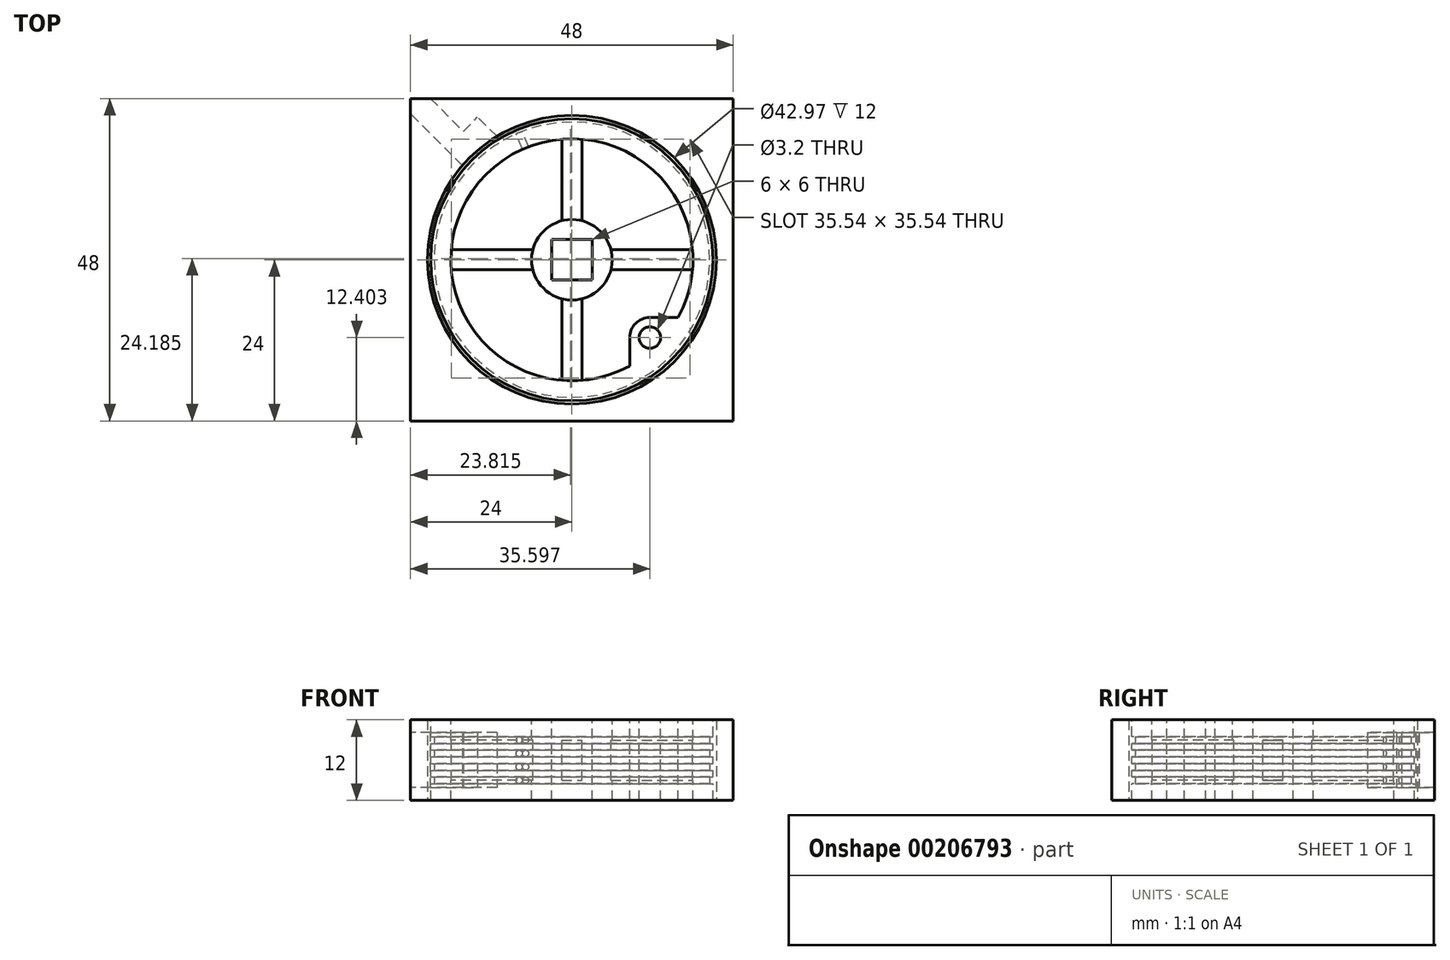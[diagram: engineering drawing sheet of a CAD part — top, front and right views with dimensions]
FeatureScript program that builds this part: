
annotation { "Feature Type Name" : "Feature", "Feature Type Description" : "" }
export const myFeature = defineFeature(function(context is Context, id is Id, definition is map)
    precondition{}
    {
        {
            var Q0;
            Q0=qCreatedBy(makeId("Front.planeOp"),FACE);
            var sketch = newSketch(context, id + "F0", { "sketchPlane" : qUnion([Q0])});
            skLineSegment(sketch, "E0", {"start": v(0, 69.7) * mm, "end": v(0, -33.75) * mm, "construction": true});
            skSolve(sketch);
        }
        {
            var Q0;
            Q0=sQuery(id+"F0.wireOp",EDGE,"E0");
            cPlane(context, id + "F1", {"entities" : qUnion([Q0]), "cplaneType" : CPlaneType.LINE_ANGLE, "offset" : 25 * mm, "angle" : 45 * degree, "width" : 150 * mm, "height" : 150 * mm});
        }
        {
            var Q0;
            Q0=qCreatedBy(makeId("Top.planeOp"),FACE);
            var sketch = newSketch(context, id + "F2", { "sketchPlane" : qUnion([Q0])});
            skCircle(sketch, "E1", {"center": v(0, 0) * mm, "radius": 21 * mm, "construction": true});
            skLineSegment(sketch, "E2.bottom", {"start": v(-24, 24) * mm, "end": v(24, 24) * mm, "construction": true});
            skLineSegment(sketch, "E2.top", {"start": v(-24, -24) * mm, "end": v(24, -24) * mm, "construction": true});
            skLineSegment(sketch, "E2.left", {"start": v(-24, 24) * mm, "end": v(-24, -24) * mm, "construction": true});
            skLineSegment(sketch, "E2.right", {"start": v(24, 24) * mm, "end": v(24, -24) * mm, "construction": true});
            skLineSegment(sketch, "E3", {"start": v(-58.08, 0) * mm, "end": v(67.15, 0) * mm, "construction": true});
            skLineSegment(sketch, "E4", {"start": v(0, 56.42) * mm, "end": v(0, -59.69) * mm, "construction": true});
            skPoint(sketch, "E5", {"position": v(21, 0) * mm});
            skSolve(sketch);
        }
        {
            var Q0;
            Q0=qCreatedBy(makeId("Top.planeOp"),FACE);
            var sketch = newSketch(context, id + "F3", { "sketchPlane" : qUnion([Q0])});
            skLineSegment(sketch, "E6.0", {"start": v(-24, 24) * mm, "end": v(24, 24) * mm});
            skLineSegment(sketch, "E6.1", {"start": v(-24, 24) * mm, "end": v(-24, -24) * mm});
            skLineSegment(sketch, "E6.2", {"start": v(-24, -24) * mm, "end": v(24, -24) * mm});
            skLineSegment(sketch, "E6.3", {"start": v(24, 24) * mm, "end": v(24, -24) * mm});
            skCircle(sketch, "E7", {"center": v(0, 0) * mm, "radius": 21.48 * mm});
            skLineSegment(sketch, "E8", {"start": v(-24, 24) * mm, "end": v(24, -24) * mm, "construction": true});
            skPoint(sketch, "E9", {"position": v(-15.2, 15.2) * mm});
            skSolve(sketch);
        }
        {
            var Q0;
            Q0=makeQuery(id+"F3.imprint","IMPRINT",FACE,{"disambiguationData":[TD([[makeQuery(id+"F3.imprint","IMPRINT",EDGE,{"derivedFrom":sQuery(id+"F3.wireOp",EDGE,"E6.0")}),-1.0]])]});
            extrude(context, id + "F4", {"entities" : qUnion([Q0]), "depth" : 12 * mm});
        }
        {
            var Q0;
            Q0=qCreatedBy(id+"F1.planeOp",FACE);
            var Q1;
            Q1=sQuery(id+"F3.wireOp",VERTEX,"E9");
            cPlane(context, id + "F5", {"entities" : qUnion([Q0, Q1]), "cplaneType" : CPlaneType.PLANE_POINT, "offset" : 25 * mm, "width" : 150 * mm, "height" : 150 * mm});
        }
        {
            var Q0;
            Q0=qCreatedBy(id+"F5.planeOp",FACE);
            cPlane(context, id + "F6", {"entities" : qUnion([Q0]), "cplaneType" : CPlaneType.OFFSET, "offset" : 3.45 * mm, "width" : 150 * mm, "height" : 150 * mm});
        }
        {
            var Q0;
            Q0=qCreatedBy(id+"F6.planeOp",FACE);
            var sketch = newSketch(context, id + "F7", { "sketchPlane" : qUnion([Q0])});
            skLineSegment(sketch, "E10.bottom", {"start": v(1.6, 10.1) * mm, "end": v(-5.1, 10.1) * mm});
            skLineSegment(sketch, "E10.top", {"start": v(1.6, 1.9) * mm, "end": v(-5.1, 1.9) * mm});
            skLineSegment(sketch, "E10.left", {"start": v(1.6, 10.1) * mm, "end": v(1.6, 1.9) * mm});
            skLineSegment(sketch, "E10.right", {"start": v(-5.1, 10.1) * mm, "end": v(-5.1, 1.9) * mm});
            skLineSegment(sketch, "E11", {"start": v(0, 12.62) * mm, "end": v(0, -16.36) * mm, "construction": true});
            skLineSegment(sketch, "E12", {"start": v(12.81, 6) * mm, "end": v(-12.63, 6) * mm, "construction": true});
            skSolve(sketch);
        }
        {
            var Q0;
            Q0 = qSketchRegion(id + "F7", true);
            var Q1;
            Q1=makeQuery(id+"F4.opExtrude","SWEPT_FACE",FACE,{"disambiguationData":[OSD([sQuery(id+"F3.wireOp",EDGE,"E7")])]});
            extrude(context, id + "F8", {"entities" : qUnion([Q0]), "operationType" : NewBodyOperationType.REMOVE, "endBound" : BoundingType.UP_TO_SURFACE, "oppositeDirection" : true, "endBoundEntityFace" : qUnion([Q1]), "depth" : 25 * mm});
        }
        {
            var Q0;
            Q0=makeQuery(id+"F8.boolean.opBoolean","COPY",FACE,{"derivedFrom":makeQuery(id+"F8.opExtrude","CAP_FACE",FACE,{"disambiguationData":[OSD([sQuery(id+"F7.wireOp",EDGE,"E10.bottom"),sQuery(id+"F7.wireOp",EDGE,"E10.top"),sQuery(id+"F7.wireOp",EDGE,"E10.left"),sQuery(id+"F7.wireOp",EDGE,"E10.right")])],"isStart":true})});
            var sketch = newSketch(context, id + "F9", { "sketchPlane" : qUnion([Q0])});
            skLineSegment(sketch, "E13.bottom", {"start": v(-1.6, 10.1) * mm, "end": v(2.1, 10.1) * mm});
            skLineSegment(sketch, "E13.top", {"start": v(-1.6, 1.9) * mm, "end": v(2.1, 1.9) * mm});
            skLineSegment(sketch, "E13.left", {"start": v(-1.6, 10.1) * mm, "end": v(-1.6, 1.9) * mm});
            skLineSegment(sketch, "E13.right", {"start": v(2.1, 10.1) * mm, "end": v(2.1, 1.9) * mm});
            skSolve(sketch);
        }
        {
            var Q0;
            Q0 = qSketchRegion(id + "F9", true);
            extrude(context, id + "F10", {"entities" : qUnion([Q0]), "operationType" : NewBodyOperationType.REMOVE, "endBound" : BoundingType.THROUGH_ALL, "oppositeDirection" : true, "depth" : 25 * mm});
        }
        {
            var Q0;
            Q0=qCreatedBy(makeId("Front.planeOp"),FACE);
            var sketch = newSketch(context, id + "F11", { "sketchPlane" : qUnion([Q0])});
            skLineSegment(sketch, "E14.left", {"start": v(0, 0) * mm, "end": v(0, 6) * mm});
            skLineSegment(sketch, "E14.right", {"start": v(21, 0) * mm, "end": v(21, 6) * mm});
            skLineSegment(sketch, "E15", {"start": v(-9.36, 6) * mm, "end": v(27.08, 6) * mm, "construction": true});
            skLineSegment(sketch, "E16", {"start": v(0, 0) * mm, "end": v(6, 0) * mm});
            skLineSegment(sketch, "E17", {"start": v(6, 0) * mm, "end": v(6, 3) * mm});
            skLineSegment(sketch, "E18", {"start": v(6, 3) * mm, "end": v(18, 3) * mm});
            skLineSegment(sketch, "E19", {"start": v(18, 3) * mm, "end": v(18, 0) * mm});
            skLineSegment(sketch, "E20", {"start": v(18, 0) * mm, "end": v(21, 0) * mm});
            skLineSegment(sketch, "E21.MirrorCS", {"start": v(0, 12) * mm, "end": v(0, 6) * mm});
            skLineSegment(sketch, "E22.MirrorCS", {"start": v(21, 12) * mm, "end": v(21, 6) * mm});
            skLineSegment(sketch, "E23.MirrorCS", {"start": v(18, 12) * mm, "end": v(21, 12) * mm});
            skLineSegment(sketch, "E24.MirrorCS", {"start": v(6, 12) * mm, "end": v(6, 9) * mm});
            skLineSegment(sketch, "E25.MirrorCS", {"start": v(18, 9) * mm, "end": v(18, 12) * mm});
            skLineSegment(sketch, "E26.MirrorCS", {"start": v(0, 12) * mm, "end": v(6, 12) * mm});
            skLineSegment(sketch, "E27.MirrorCS", {"start": v(6, 9) * mm, "end": v(18, 9) * mm});
            skSolve(sketch);
        }
        {
            var Q0;
            Q0=makeQuery(id+"F11.imprint","IMPRINT",FACE,{"disambiguationData":[TD([[makeQuery(id+"F11.imprint","IMPRINT",EDGE,{"derivedFrom":sQuery(id+"F11.wireOp",EDGE,"E14.left")}),-1.0]])]});
            var Q1;
            Q1=sQuery(id+"F0.wireOp",EDGE,"E0");
            revolve(context, id + "F12", {"entities" : qUnion([Q0]), "axis" : qUnion([Q1]), "revolveType" : RevolveType.FULL});
        }
        {
            var Q0;
            Q0=makeQuery(id+"F12.opRevolve","SWEPT_FACE",FACE,{"disambiguationData":[OSD([sQuery(id+"F11.wireOp",EDGE,"E26.MirrorCS")])]});
            var sketch = newSketch(context, id + "F13", { "sketchPlane" : qUnion([Q0])});
            skCircle(sketch, "E28.0", {"center": v(0, 0) * mm, "radius": 18 * mm});
            skCircle(sketch, "E29.0", {"center": v(0, 0) * mm, "radius": 6 * mm});
            skLineSegment(sketch, "E30", {"start": v(-1.5, 5.8) * mm, "end": v(-1.5, 17.94) * mm});
            skLineSegment(sketch, "E31", {"start": v(1.5, 5.8) * mm, "end": v(1.5, 17.94) * mm});
            skLineSegment(sketch, "E32.1.0", {"start": v(-5.8, -1.5) * mm, "end": v(-17.94, -1.5) * mm});
            skLineSegment(sketch, "E32.1.1", {"start": v(-5.8, 1.5) * mm, "end": v(-17.94, 1.5) * mm});
            skLineSegment(sketch, "E32.2.0", {"start": v(1.5, -5.8) * mm, "end": v(1.5, -17.94) * mm});
            skLineSegment(sketch, "E32.2.1", {"start": v(-1.5, -5.8) * mm, "end": v(-1.5, -17.94) * mm});
            skLineSegment(sketch, "E32.3.0", {"start": v(5.8, 1.5) * mm, "end": v(17.94, 1.5) * mm});
            skLineSegment(sketch, "E32.3.1", {"start": v(5.8, -1.5) * mm, "end": v(17.94, -1.5) * mm});
            skSolve(sketch);
        }
        {
            var Q0;
            {var subQ0=sQuery(id+"F13.wireOp",EDGE,"E30");Q0=makeQuery(id+"F13.imprint","IMPRINT",FACE,{"disambiguationData":[TD([[makeQuery(id+"F13.imprint","IMPRINT",EDGE,{"derivedFrom":subQ0}),1.0]])]});}
            var Q1;
            {var subQ0=sQuery(id+"F13.wireOp",EDGE,"E31");Q1=makeQuery(id+"F13.imprint","IMPRINT",FACE,{"disambiguationData":[TD([[makeQuery(id+"F13.imprint","IMPRINT",EDGE,{"derivedFrom":subQ0}),-1.0]])]});}
            var Q2;
            {var subQ0=sQuery(id+"F13.wireOp",EDGE,"E32.2.0");Q2=makeQuery(id+"F13.imprint","IMPRINT",FACE,{"disambiguationData":[TD([[makeQuery(id+"F13.imprint","IMPRINT",EDGE,{"derivedFrom":subQ0}),1.0]])]});}
            var Q3;
            {var subQ0=sQuery(id+"F13.wireOp",EDGE,"E32.1.0");Q3=makeQuery(id+"F13.imprint","IMPRINT",FACE,{"disambiguationData":[TD([[makeQuery(id+"F13.imprint","IMPRINT",EDGE,{"derivedFrom":subQ0}),1.0]])]});}
            var Q4;
            Q4=makeQuery(id+"F12.opRevolve","SWEPT_FACE",FACE,{"disambiguationData":[OSD([sQuery(id+"F11.wireOp",EDGE,"E16")])]});
            extrude(context, id + "F14", {"entities" : qUnion([Q0, Q1, Q2, Q3]), "operationType" : NewBodyOperationType.REMOVE, "endBound" : BoundingType.UP_TO_SURFACE, "oppositeDirection" : true, "endBoundEntityFace" : qUnion([Q4]), "depth" : 25 * mm});
        }
        {
            var Q0;
            Q0=makeQuery(id+"F12.opRevolve","SWEPT_FACE",FACE,{"disambiguationData":[OSD([sQuery(id+"F11.wireOp",EDGE,"E23.MirrorCS")])]});
            var sketch = newSketch(context, id + "F15", { "sketchPlane" : qUnion([Q0])});
            skArc(sketch, "E33", {"start": v(11.6, -8.6) * mm, "mid": v(9.48, -9.48) * mm, "end": v(8.6, -11.6) * mm});
            skLineSegment(sketch, "E34", {"start": v(8.6, -11.6) * mm, "end": v(8.6, -19.16) * mm});
            skLineSegment(sketch, "E35", {"start": v(11.6, -8.6) * mm, "end": v(19.16, -8.6) * mm});
            skCircle(sketch, "E36", {"center": v(11.6, -11.6) * mm, "radius": 1.6 * mm});
            skArc(sketch, "E37.0", {"start": v(8.6, -19.16) * mm, "mid": v(14.85, -14.85) * mm, "end": v(19.16, -8.6) * mm});
            skSolve(sketch);
        }
        {
            var Q0;
            Q0 = qSketchRegion(id + "F15", true);
            var Q1;
            Q1=makeQuery(id+"F12.opRevolve","SWEPT_FACE",FACE,{"disambiguationData":[OSD([sQuery(id+"F11.wireOp",EDGE,"E20")])]});
            extrude(context, id + "F16", {"entities" : qUnion([Q0]), "operationType" : NewBodyOperationType.ADD, "endBound" : BoundingType.UP_TO_SURFACE, "oppositeDirection" : true, "endBoundEntityFace" : qUnion([Q1]), "depth" : 25 * mm});
        }
        {
            var Q0;
            Q0=makeQuery(id+"F12.opRevolve","SWEPT_FACE",FACE,{"disambiguationData":[OSD([sQuery(id+"F11.wireOp",EDGE,"E26.MirrorCS")])]});
            var sketch = newSketch(context, id + "F17", { "sketchPlane" : qUnion([Q0])});
            skLineSegment(sketch, "E38.bottom", {"start": v(-3, -3) * mm, "end": v(3, -3) * mm});
            skLineSegment(sketch, "E38.top", {"start": v(-3, 3) * mm, "end": v(3, 3) * mm});
            skLineSegment(sketch, "E38.left", {"start": v(-3, -3) * mm, "end": v(-3, 3) * mm});
            skLineSegment(sketch, "E38.right", {"start": v(3, -3) * mm, "end": v(3, 3) * mm});
            skSolve(sketch);
        }
        {
            var Q0;
            Q0 = qSketchRegion(id + "F17", true);
            var Q1;
            Q1=makeQuery(id+"F12.opRevolve","SWEPT_FACE",FACE,{"disambiguationData":[OSD([sQuery(id+"F11.wireOp",EDGE,"E16")])]});
            extrude(context, id + "F18", {"entities" : qUnion([Q0]), "operationType" : NewBodyOperationType.REMOVE, "endBound" : BoundingType.UP_TO_SURFACE, "oppositeDirection" : true, "endBoundEntityFace" : qUnion([Q1]), "depth" : 25 * mm});
        }
        {
            var Q0;
            Q0=qCreatedBy(makeId("Front.planeOp"),FACE);
            var sketch = newSketch(context, id + "F19", { "sketchPlane" : qUnion([Q0])});
            skLineSegment(sketch, "E39", {"start": v(6.35, 6) * mm, "end": v(33.6, 6) * mm, "construction": true});
            skLineSegment(sketch, "E40.bottom", {"start": v(20.5, 9.5) * mm, "end": v(21, 9.5) * mm});
            skLineSegment(sketch, "E40.top", {"start": v(20.5, 8.5) * mm, "end": v(21, 8.5) * mm});
            skLineSegment(sketch, "E40.left", {"start": v(20.5, 9.5) * mm, "end": v(20.5, 8.5) * mm});
            skLineSegment(sketch, "E40.right", {"start": v(21, 9.5) * mm, "end": v(21, 8.5) * mm});
            skLineSegment(sketch, "E41", {"start": v(13.97, 9) * mm, "end": v(28.19, 9) * mm, "construction": true});
            skLineSegment(sketch, "E42.MirrorCS", {"start": v(20.5, 8.5) * mm, "end": v(20.5, 9.5) * mm});
            skLineSegment(sketch, "E43.MirrorCS", {"start": v(21, 8.5) * mm, "end": v(21, 9.5) * mm});
            skLineSegment(sketch, "E44", {"start": v(21, 12.24) * mm, "end": v(21, 3.07) * mm, "construction": true});
            skLineSegment(sketch, "E45", {"start": v(12.13, 7) * mm, "end": v(30.38, 7) * mm, "construction": true});
            skLineSegment(sketch, "E46.1.0.0", {"start": v(20.5, 6.5) * mm, "end": v(20.5, 7.5) * mm});
            skLineSegment(sketch, "E46.1.0.1", {"start": v(21, 6.5) * mm, "end": v(21, 7.5) * mm});
            skLineSegment(sketch, "E46.1.0.2", {"start": v(20.5, 6.5) * mm, "end": v(21, 6.5) * mm});
            skLineSegment(sketch, "E46.1.0.3", {"start": v(20.5, 7.5) * mm, "end": v(21, 7.5) * mm});
            skLineSegment(sketch, "E46.1.0.4", {"start": v(20.5, 7.5) * mm, "end": v(21, 7.5) * mm});
            skLineSegment(sketch, "E46.1.0.5", {"start": v(20.5, 6.5) * mm, "end": v(21, 6.5) * mm});
            skLineSegment(sketch, "E46.1.0.6", {"start": v(20.5, 7.5) * mm, "end": v(20.5, 6.5) * mm});
            skLineSegment(sketch, "E46.1.0.7", {"start": v(21, 7.5) * mm, "end": v(21, 6.5) * mm});
            skLineSegment(sketch, "E46.2.0.0", {"start": v(20.5, 4.5) * mm, "end": v(20.5, 5.5) * mm});
            skLineSegment(sketch, "E46.2.0.1", {"start": v(21, 4.5) * mm, "end": v(21, 5.5) * mm});
            skLineSegment(sketch, "E46.2.0.2", {"start": v(20.5, 4.5) * mm, "end": v(21, 4.5) * mm});
            skLineSegment(sketch, "E46.2.0.3", {"start": v(20.5, 5.5) * mm, "end": v(21, 5.5) * mm});
            skLineSegment(sketch, "E46.2.0.4", {"start": v(20.5, 5.5) * mm, "end": v(21, 5.5) * mm});
            skLineSegment(sketch, "E46.2.0.5", {"start": v(20.5, 4.5) * mm, "end": v(21, 4.5) * mm});
            skLineSegment(sketch, "E46.2.0.6", {"start": v(20.5, 5.5) * mm, "end": v(20.5, 4.5) * mm});
            skLineSegment(sketch, "E46.2.0.7", {"start": v(21, 5.5) * mm, "end": v(21, 4.5) * mm});
            skLineSegment(sketch, "E46.3.0.0", {"start": v(20.5, 2.5) * mm, "end": v(20.5, 3.5) * mm});
            skLineSegment(sketch, "E46.3.0.1", {"start": v(21, 2.5) * mm, "end": v(21, 3.5) * mm});
            skLineSegment(sketch, "E46.3.0.2", {"start": v(20.5, 2.5) * mm, "end": v(21, 2.5) * mm});
            skLineSegment(sketch, "E46.3.0.3", {"start": v(20.5, 3.5) * mm, "end": v(21, 3.5) * mm});
            skLineSegment(sketch, "E46.3.0.4", {"start": v(20.5, 3.5) * mm, "end": v(21, 3.5) * mm});
            skLineSegment(sketch, "E46.3.0.5", {"start": v(20.5, 2.5) * mm, "end": v(21, 2.5) * mm});
            skLineSegment(sketch, "E46.3.0.6", {"start": v(20.5, 3.5) * mm, "end": v(20.5, 2.5) * mm});
            skLineSegment(sketch, "E46.3.0.7", {"start": v(21, 3.5) * mm, "end": v(21, 2.5) * mm});
            skLineSegment(sketch, "E46.direction1", {"start": v(20.5, 8.5) * mm, "end": v(20.5, 6.5) * mm, "construction": true});
            skSolve(sketch);
        }
        {
            var Q0;
            Q0 = qSketchRegion(id + "F19", true);
            var Q1;
            Q1=sQuery(id+"F0.wireOp",EDGE,"E0");
            revolve(context, id + "F20", {"operationType" : NewBodyOperationType.REMOVE, "entities" : qUnion([Q0]), "axis" : qUnion([Q1]), "revolveType" : RevolveType.FULL, "oppositeDirection" : true});
        }
        {
            var Q0;
            Q0=qCreatedBy(makeId("Top.planeOp"),FACE);
            var sketch = newSketch(context, id + "F21", { "sketchPlane" : qUnion([Q0])});
            skLineSegment(sketch, "E47", {"start": v(0, 0) * mm, "end": v(-12.81, 30.93) * mm, "construction": true});
            skPoint(sketch, "E48", {"position": v(-8.04, 19.4) * mm});
            skSolve(sketch);
        }
        {
            var Q0;
            Q0=sQuery(id+"F0.wireOp",EDGE,"E0");
            cPlane(context, id + "F22", {"entities" : qUnion([Q0]), "cplaneType" : CPlaneType.LINE_ANGLE, "offset" : 25 * mm, "angle" : 67.5 * degree, "width" : 150 * mm, "height" : 150 * mm});
        }
        {
            var Q0;
            Q0=qCreatedBy(id+"F22.planeOp",FACE);
            var Q1;
            Q1=sQuery(id+"F21.wireOp",VERTEX,"E48");
            cPlane(context, id + "F23", {"entities" : qUnion([Q0, Q1]), "cplaneType" : CPlaneType.PLANE_POINT, "offset" : 25 * mm, "width" : 150 * mm, "height" : 150 * mm});
        }
        {
            var Q0;
            Q0=qCreatedBy(id+"F23.planeOp",FACE);
            var sketch = newSketch(context, id + "F24", { "sketchPlane" : qUnion([Q0])});
            skLineSegment(sketch, "E49", {"start": v(-4.54, 3) * mm, "end": v(5.72, 3) * mm, "construction": true});
            skCircle(sketch, "E50", {"center": v(0, 3) * mm, "radius": 0.5 * mm});
            skCircle(sketch, "E51.1.0.0", {"center": v(0, 5) * mm, "radius": 0.5 * mm});
            skCircle(sketch, "E51.2.0.0", {"center": v(0, 7) * mm, "radius": 0.5 * mm});
            skCircle(sketch, "E51.3.0.0", {"center": v(0, 9) * mm, "radius": 0.5 * mm});
            skLineSegment(sketch, "E51.direction1", {"start": v(0, 3) * mm, "end": v(0, 5) * mm, "construction": true});
            skSolve(sketch);
        }
        {
            var Q0;
            Q0 = qSketchRegion(id + "F24", true);
            var Q1;
            {var subQ3=sQuery(id+"F13.wireOp",EDGE,"E31");var subQ11=sQuery(id+"F13.wireOp",EDGE,"E30");var subQ12=makeQuery(id+"F14.boolean.opBoolean","COPY",FACE,{"derivedFrom":makeQuery(id+"F14.opExtrude","SWEPT_FACE",FACE,{"disambiguationData":[OSD([subQ11])]})});var subQ26=sQuery(id+"F13.wireOp",EDGE,"E32.1.0");var subQ28=sQuery(id+"F13.wireOp",EDGE,"E28.0");Q1=makeQuery(id+"F0W7oMUfATiE3Vz_2.3.F16.boolean.opBoolean","SPLIT",FACE,{"disambiguationData":[TD([subQ12])],"derivedFrom":makeQuery(id+"F0W7oMUfATiE3Vz_2.2.F16.boolean.opBoolean","SPLIT",FACE,{"disambiguationData":[TD([subQ12])],"derivedFrom":makeQuery(id+"F0W7oMUfATiE3Vz_2.1.F16.boolean.opBoolean","SPLIT",FACE,{"disambiguationData":[TD([subQ12])],"derivedFrom":makeQuery(id+"F14.boolean.opBoolean","MERGE",FACE,{"derivedFrom":[makeQuery(id+"F12.opRevolve","SWEPT_FACE",FACE,{"disambiguationData":[OSD([sQuery(id+"F11.wireOp",EDGE,"E19")])]}),makeQuery(id+"F12.opRevolve","SWEPT_FACE",FACE,{"disambiguationData":[OSD([sQuery(id+"F11.wireOp",EDGE,"E25.MirrorCS")])]}),makeQuery(id+"F14.opExtrude","SWEPT_FACE",FACE,{"disambiguationData":[OSD([subQ28]),TDD([makeQuery(id+"F13.imprint","IMPRINT",EDGE,{"disambiguationData":[TD([[makeQuery(id+"F13.imprint","INTERSECT",VERTEX,{"derivedFrom":[subQ28,subQ3]}),1.0]])],"derivedFrom":subQ28})])]}),makeQuery(id+"F14.opExtrude","SWEPT_FACE",FACE,{"disambiguationData":[OSD([subQ28]),TDD([makeQuery(id+"F13.imprint","IMPRINT",EDGE,{"disambiguationData":[TD([[makeQuery(id+"F13.imprint","INTERSECT",VERTEX,{"derivedFrom":[subQ28,subQ11]}),-1.0]])],"derivedFrom":subQ28})])]}),makeQuery(id+"F14.opExtrude","SWEPT_FACE",FACE,{"disambiguationData":[OSD([subQ28]),TDD([makeQuery(id+"F13.imprint","IMPRINT",EDGE,{"disambiguationData":[TD([[makeQuery(id+"F13.imprint","INTERSECT",VERTEX,{"derivedFrom":[subQ28,subQ26]}),-1.0]])],"derivedFrom":subQ28})])]}),makeQuery(id+"F14.opExtrude","SWEPT_FACE",FACE,{"disambiguationData":[OSD([subQ28]),TDD([makeQuery(id+"F13.imprint","IMPRINT",EDGE,{"disambiguationData":[TD([[makeQuery(id+"F13.imprint","INTERSECT",VERTEX,{"derivedFrom":[subQ28,sQuery(id+"F13.wireOp",EDGE,"E32.2.0")]}),-1.0]])],"derivedFrom":subQ28})])]})]})})})});}
            extrude(context, id + "F25", {"entities" : qUnion([Q0]), "operationType" : NewBodyOperationType.REMOVE, "endBound" : BoundingType.UP_TO_SURFACE, "oppositeDirection" : true, "endBoundEntityFace" : qUnion([Q1]), "depth" : 25 * mm});
        }
    });
